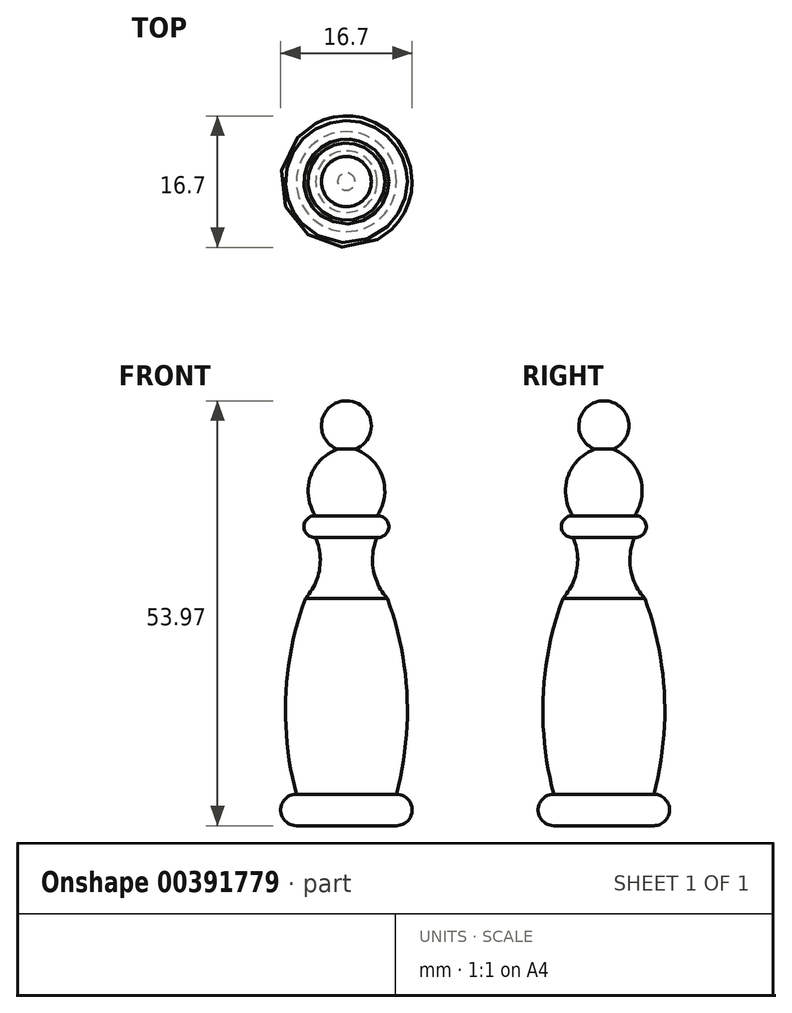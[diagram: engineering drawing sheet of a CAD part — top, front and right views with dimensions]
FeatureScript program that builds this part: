
annotation { "Feature Type Name" : "Feature", "Feature Type Description" : "" }
export const myFeature = defineFeature(function(context is Context, id is Id, definition is map)
    precondition{}
    {
        {
            var Q0;
            Q0=qCreatedBy(makeId("Front.planeOp"),FACE);
            var sketch = newSketch(context, id + "F0", { "sketchPlane" : qUnion([Q0])});
            skArc(sketch, "E0", {"start": v(1.1, 22.42) * mm, "mid": v(3.13, 25.96) * mm, "end": v(0, 28.58) * mm});
            skArc(sketch, "E1", {"start": v(3.9, 13.96) * mm, "mid": v(4.6, 18.88) * mm, "end": v(1.1, 22.42) * mm});
            skArc(sketch, "E2", {"start": v(3.9, 11.2) * mm, "mid": v(5.4, 12.58) * mm, "end": v(3.9, 13.96) * mm});
            skArc(sketch, "E3", {"start": v(3.9, 11.2) * mm, "mid": v(3.41, 7.15) * mm, "end": v(5.2, 3.48) * mm});
            skLineSegment(sketch, "E4", {"start": v(0, -25.4) * mm, "end": v(6.35, -25.4) * mm});
            skArc(sketch, "E5", {"start": v(6.35, -25.4) * mm, "mid": v(8.35, -23.4) * mm, "end": v(6.35, -21.4) * mm});
            skArc(sketch, "E6", {"start": v(6.35, -21.4) * mm, "mid": v(7.7, -8.87) * mm, "end": v(5.2, 3.48) * mm});
            skLineSegment(sketch, "E7", {"start": v(0, 28.58) * mm, "end": v(0, -25.4) * mm});
            skSolve(sketch);
        }
        {
            var Q0;
            Q0=makeQuery(id+"F0.imprint","IMPRINT",FACE,{"disambiguationData":[TD([[makeQuery(id+"F0.imprint","IMPRINT",EDGE,{"derivedFrom":sQuery(id+"F0.wireOp",EDGE,"E0")}),1.0]])]});
            var Q1;
            Q1=sQuery(id+"F0.wireOp",EDGE,"E7");
            revolve(context, id + "F1", {"entities" : qUnion([Q0]), "axis" : qUnion([Q1]), "revolveType" : RevolveType.FULL});
        }
    });
